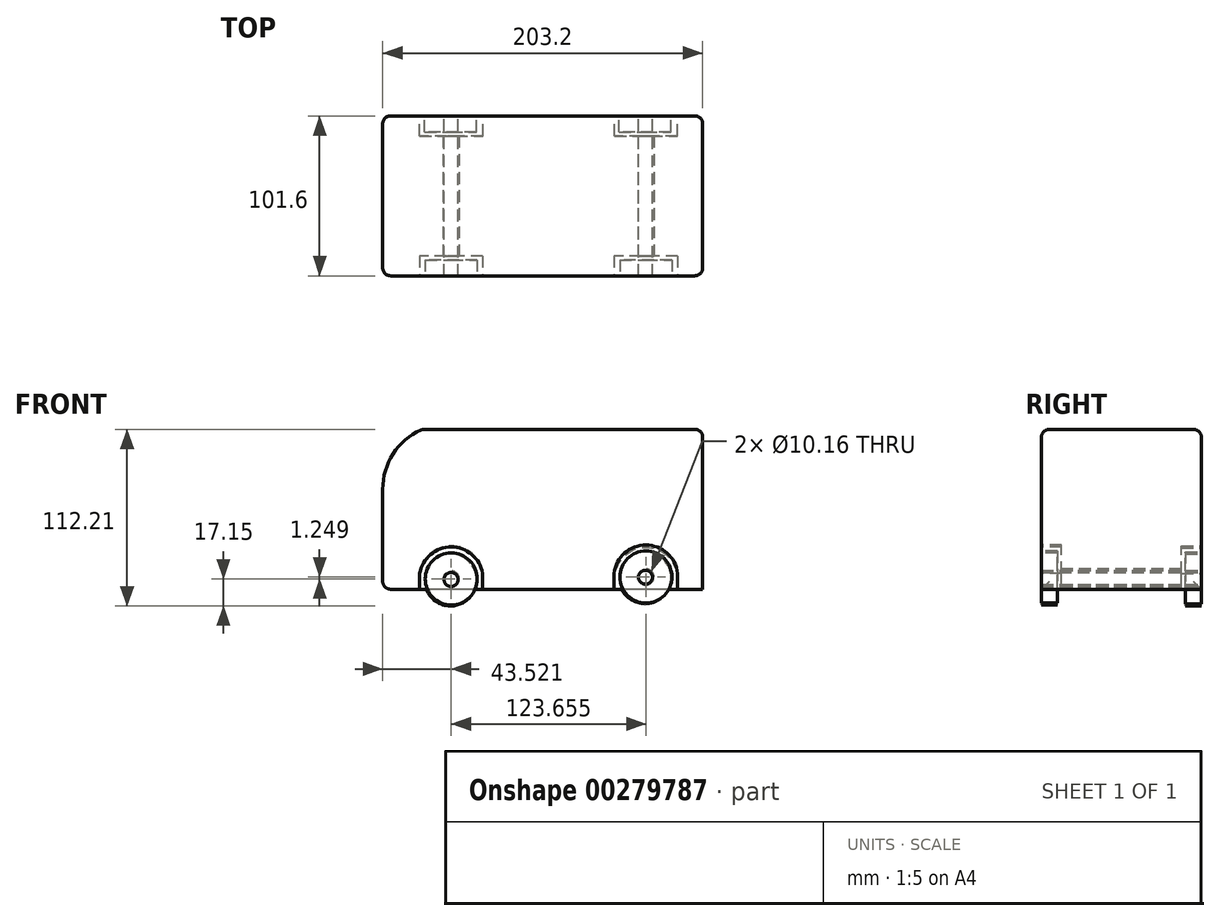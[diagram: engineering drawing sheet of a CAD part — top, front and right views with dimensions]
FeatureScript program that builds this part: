
annotation { "Feature Type Name" : "Feature", "Feature Type Description" : "" }
export const myFeature = defineFeature(function(context is Context, id is Id, definition is map)
    precondition{}
    {
        {
            var Q0;
            Q0=qCreatedBy(makeId("Front.planeOp"),FACE);
            var sketch = newSketch(context, id + "F0", { "sketchPlane" : qUnion([Q0])});
            skLineSegment(sketch, "E0", {"start": v(58.5, 0) * mm, "end": v(58.5, 50.8) * mm});
            skLineSegment(sketch, "E1.MirrorCS", {"start": v(58.5, 0) * mm, "end": v(58.5, -50.8) * mm});
            skLineSegment(sketch, "E2", {"start": v(58.5, 50.8) * mm, "end": v(-119.3, 50.8) * mm});
            skLineSegment(sketch, "E3", {"start": v(58.5, -50.8) * mm, "end": v(-144.7, -50.8) * mm});
            skLineSegment(sketch, "E4", {"start": v(-144.7, -50.8) * mm, "end": v(-144.7, 12.7) * mm});
            skArc(sketch, "E5", {"start": v(-119.3, 50.8) * mm, "mid": v(-137.76, 35.6) * mm, "end": v(-144.7, 12.7) * mm});
            skSolve(sketch);
        }
        {
            var Q0;
            Q0 = qSketchRegion(id + "F0", true);
            extrude(context, id + "F1", {"entities" : qUnion([Q0]), "depth" : 101.6 * mm});
        }
        {
            var Q0;
            Q0=makeQuery(id+"F1.opExtrude","CAP_EDGE",EDGE,{"disambiguationData":[OSD([sQuery(id+"F0.wireOp",EDGE,"E2")])],"isStart":true});
            var Q1;
            Q1=makeQuery(id+"F1.opExtrude","SWEPT_EDGE",EDGE,{"disambiguationData":[OSD([sQuery(id+"F0.wireOp",EDGE,"E2"),sQuery(id+"F0.wireOp",EDGE,"E5")])]});
            var Q2;
            Q2=makeQuery(id+"F1.opExtrude","CAP_EDGE",EDGE,{"disambiguationData":[OSD([sQuery(id+"F0.wireOp",EDGE,"E5")])],"isStart":true});
            var Q3;
            Q3=makeQuery(id+"F1.opExtrude","CAP_EDGE",EDGE,{"disambiguationData":[OSD([sQuery(id+"F0.wireOp",EDGE,"E4")])],"isStart":true});
            var Q4;
            Q4=makeQuery(id+"F1.opExtrude","CAP_EDGE",EDGE,{"disambiguationData":[OSD([sQuery(id+"F0.wireOp",EDGE,"E4")])],"isStart":false});
            var Q5;
            Q5=makeQuery(id+"F1.opExtrude","CAP_EDGE",EDGE,{"disambiguationData":[OSD([sQuery(id+"F0.wireOp",EDGE,"E5")])],"isStart":false});
            var Q6;
            Q6=makeQuery(id+"F1.opExtrude","CAP_EDGE",EDGE,{"disambiguationData":[OSD([sQuery(id+"F0.wireOp",EDGE,"E2")])],"isStart":false});
            var Q7;
            Q7=makeQuery(id+"F1.opExtrude","SWEPT_EDGE",EDGE,{"disambiguationData":[OSD([sQuery(id+"F0.wireOp",EDGE,"E0"),sQuery(id+"F0.wireOp",EDGE,"E2")])]});
            var Q8;
            Q8=makeQuery(id+"F1.opExtrude","CAP_EDGE",EDGE,{"disambiguationData":[OSD([sQuery(id+"F0.wireOp",EDGE,"E0"),sQuery(id+"F0.wireOp",EDGE,"E1.MirrorCS")])],"isStart":true});
            var Q9;
            Q9=makeQuery(id+"F1.opExtrude","CAP_EDGE",EDGE,{"disambiguationData":[OSD([sQuery(id+"F0.wireOp",EDGE,"E0"),sQuery(id+"F0.wireOp",EDGE,"E1.MirrorCS")])],"isStart":false});
            var Q10;
            Q10=makeQuery(id+"F1.opExtrude","SWEPT_EDGE",EDGE,{"disambiguationData":[OSD([sQuery(id+"F0.wireOp",EDGE,"E3"),sQuery(id+"F0.wireOp",EDGE,"E4")])]});
            fillet(context, id + "F2", {"entities" : qUnion([Q0, Q1, Q2, Q3, Q4, Q5, Q6, Q7, Q8, Q9, Q10]), "radius" : 5.08 * mm, "tangentPropagation" : true, "allowEdgeOverflow" : false});
        }
        {
            var Q0;
            Q0=makeQuery(id+"F1.opExtrude","CAP_FACE",FACE,{"disambiguationData":[OSD([sQuery(id+"F0.wireOp",EDGE,"E0"),sQuery(id+"F0.wireOp",EDGE,"E1.MirrorCS"),sQuery(id+"F0.wireOp",EDGE,"E2"),sQuery(id+"F0.wireOp",EDGE,"E3"),sQuery(id+"F0.wireOp",EDGE,"E4"),sQuery(id+"F0.wireOp",EDGE,"E5")])],"isStart":false});
            var sketch = newSketch(context, id + "F3", { "sketchPlane" : qUnion([Q0])});
            skLineSegment(sketch, "E6", {"start": v(-121.16, -50.8) * mm, "end": v(-121.16, -40.64) * mm});
            skLineSegment(sketch, "E7", {"start": v(-81.17, -50.8) * mm, "end": v(-81.17, -40.64) * mm});
            skArc(sketch, "E8", {"start": v(-81.17, -40.64) * mm, "mid": v(-101.17, -23.94) * mm, "end": v(-121.16, -40.64) * mm});
            skLineSegment(sketch, "E9", {"start": v(2.3, -50.8) * mm, "end": v(2.3, -40.64) * mm});
            skLineSegment(sketch, "E10", {"start": v(42.67, -50.8) * mm, "end": v(42.67, -40.64) * mm});
            skArc(sketch, "E11", {"start": v(42.67, -40.64) * mm, "mid": v(22.49, -22.7) * mm, "end": v(2.3, -40.64) * mm});
            skCircle(sketch, "E12", {"center": v(-101.17, -44.26) * mm, "radius": 5.08 * mm});
            skCircle(sketch, "E13", {"center": v(22.49, -43.01) * mm, "radius": 5.08 * mm});
            skSolve(sketch);
        }
        {
            var Q0;
            {var subQ1=sQuery(id+"F3.wireOp",EDGE,"E6");Q0=makeQuery(id+"F3.imprint","IMPRINT",FACE,{"disambiguationData":[TD([[makeQuery(id+"F3.imprint","IMPRINT",EDGE,{"derivedFrom":subQ1}),-1.0]])]});}
            var Q1;
            {var subQ0=sQuery(id+"F3.wireOp",EDGE,"E9");Q1=makeQuery(id+"F3.imprint","IMPRINT",FACE,{"disambiguationData":[TD([[makeQuery(id+"F3.imprint","IMPRINT",EDGE,{"derivedFrom":subQ0}),-1.0]])]});}
            extrude(context, id + "F4", {"entities" : qUnion([Q0, Q1]), "operationType" : NewBodyOperationType.REMOVE, "oppositeDirection" : true, "depth" : 12.7 * mm});
        }
        {
            var Q0;
            Q0=makeQuery(id+"F4.boolean.opBoolean","SPLIT",FACE,{"disambiguationData":[TD([makeQuery(id+"F4.opExtrude","SWEPT_FACE",FACE,{"disambiguationData":[OSD([sQuery(id+"F3.wireOp",EDGE,"E12")])]})])],"derivedFrom":makeQuery(id+"F1.opExtrude","CAP_FACE",FACE,{"disambiguationData":[OSD([sQuery(id+"F0.wireOp",EDGE,"E0"),sQuery(id+"F0.wireOp",EDGE,"E1.MirrorCS"),sQuery(id+"F0.wireOp",EDGE,"E2"),sQuery(id+"F0.wireOp",EDGE,"E3"),sQuery(id+"F0.wireOp",EDGE,"E4"),sQuery(id+"F0.wireOp",EDGE,"E5")])],"isStart":false})});
            var Q1;
            Q1=makeQuery(id+"F4.boolean.opBoolean","SPLIT",FACE,{"disambiguationData":[TD([makeQuery(id+"F4.opExtrude","SWEPT_FACE",FACE,{"disambiguationData":[OSD([sQuery(id+"F3.wireOp",EDGE,"E13")])]})])],"derivedFrom":makeQuery(id+"F1.opExtrude","CAP_FACE",FACE,{"disambiguationData":[OSD([sQuery(id+"F0.wireOp",EDGE,"E0"),sQuery(id+"F0.wireOp",EDGE,"E1.MirrorCS"),sQuery(id+"F0.wireOp",EDGE,"E2"),sQuery(id+"F0.wireOp",EDGE,"E3"),sQuery(id+"F0.wireOp",EDGE,"E4"),sQuery(id+"F0.wireOp",EDGE,"E5")])],"isStart":false})});
            extrude(context, id + "F5", {"entities" : qUnion([Q0, Q1]), "operationType" : NewBodyOperationType.REMOVE, "oppositeDirection" : true, "depth" : 101.6 * mm});
        }
        {
            var Q0;
            Q0=makeQuery(id+"F1.opExtrude","CAP_FACE",FACE,{"disambiguationData":[OSD([sQuery(id+"F0.wireOp",EDGE,"E0"),sQuery(id+"F0.wireOp",EDGE,"E1.MirrorCS"),sQuery(id+"F0.wireOp",EDGE,"E2"),sQuery(id+"F0.wireOp",EDGE,"E3"),sQuery(id+"F0.wireOp",EDGE,"E4"),sQuery(id+"F0.wireOp",EDGE,"E5")])],"isStart":true});
            var sketch = newSketch(context, id + "F6", { "sketchPlane" : qUnion([Q0])});
            skLineSegment(sketch, "E14", {"start": v(-17.58, -41.7) * mm, "end": v(-2.6, -41.7) * mm});
            skLineSegment(sketch, "E15", {"start": v(106.24, -44.03) * mm, "end": v(121.23, -44.03) * mm});
            skLineSegment(sketch, "E16", {"start": v(-27.55, -42.64) * mm, "end": v(-42.54, -42.64) * mm});
            skLineSegment(sketch, "E17", {"start": v(96.1, -44.1) * mm, "end": v(81.1, -44.1) * mm});
            skLineSegment(sketch, "E18", {"start": v(-42.54, -50.8) * mm, "end": v(-42.54, -40.64) * mm});
            skLineSegment(sketch, "E19", {"start": v(-2.6, -50.8) * mm, "end": v(-2.6, -40.64) * mm});
            skLineSegment(sketch, "E20", {"start": v(81.1, -50.8) * mm, "end": v(81.1, -40.64) * mm});
            skLineSegment(sketch, "E21", {"start": v(121.23, -50.8) * mm, "end": v(121.23, -40.64) * mm});
            skArc(sketch, "E22", {"start": v(-2.6, -40.64) * mm, "mid": v(-22.57, -24.45) * mm, "end": v(-42.54, -40.64) * mm});
            skArc(sketch, "E23", {"start": v(121.23, -40.64) * mm, "mid": v(101.17, -23.2) * mm, "end": v(81.1, -40.64) * mm});
            skSolve(sketch);
        }
        {
            var Q0;
            {var subQ1=sQuery(id+"F6.wireOp",EDGE,"E14");Q0=makeQuery(id+"F6.imprint","IMPRINT",FACE,{"disambiguationData":[TD([[makeQuery(id+"F6.imprint","IMPRINT",EDGE,{"derivedFrom":subQ1}),-1.0]])]});}
            var Q1;
            {var subQ1=sQuery(id+"F6.wireOp",EDGE,"E15");Q1=makeQuery(id+"F6.imprint","IMPRINT",FACE,{"disambiguationData":[TD([[makeQuery(id+"F6.imprint","IMPRINT",EDGE,{"derivedFrom":subQ1}),-1.0]])]});}
            var Q2;
            {var subQ4=sQuery(id+"F6.wireOp",EDGE,"E15");Q2=makeQuery(id+"F6.imprint","IMPRINT",FACE,{"disambiguationData":[TD([[makeQuery(id+"F6.imprint","IMPRINT",EDGE,{"derivedFrom":subQ4}),1.0]])]});}
            var Q3;
            {var subQ1=sQuery(id+"F6.wireOp",EDGE,"E14");Q3=makeQuery(id+"F6.imprint","IMPRINT",FACE,{"disambiguationData":[TD([[makeQuery(id+"F6.imprint","IMPRINT",EDGE,{"derivedFrom":subQ1}),1.0]])]});}
            var Q4;
            Q4=sQuery(id+"F6.wireOp",EDGE,"E19");
            var Q5;
            Q5=sQuery(id+"F6.wireOp",EDGE,"E18");
            var Q6;
            Q6=sQuery(id+"F6.wireOp",EDGE,"E22");
            var Q7;
            Q7=sQuery(id+"F6.wireOp",EDGE,"E20");
            var Q8;
            Q8=sQuery(id+"F6.wireOp",EDGE,"E23");
            var Q9;
            Q9=sQuery(id+"F6.wireOp",EDGE,"E21");
            extrude(context, id + "F7", {"entities" : qUnion([Q0, Q1, Q2, Q3]), "operationType" : NewBodyOperationType.REMOVE, "surfaceEntities" : qUnion([Q4, Q5, Q6, Q7, Q8, Q9]), "oppositeDirection" : true, "depth" : 12.7 * mm});
        }
        {
            var Q0;
            Q0=qCreatedBy(makeId("Front.planeOp"),FACE);
            var sketch = newSketch(context, id + "F8", { "sketchPlane" : qUnion([Q0])});
            skCircle(sketch, "E24", {"center": v(-101.3, -44.6) * mm, "radius": 4.45 * mm});
            skCircle(sketch, "E25", {"center": v(22.16, -43.17) * mm, "radius": 4.45 * mm});
            skSolve(sketch);
        }
        {
            var Q0;
            Q0 = qSketchRegion(id + "F8", true);
            extrude(context, id + "F9", {"entities" : qUnion([Q0]), "depth" : 101.6 * mm});
        }
        {
            var Q0;
            Q0 = qSketchRegion(id + "F8", true);
            extrude(context, id + "F10", {"entities" : qUnion([Q0]), "depth" : 101.6 * mm});
        }
        {
            var Q0;
            Q0=qCreatedBy(makeId("Front.planeOp"),FACE);
            var sketch = newSketch(context, id + "F11", { "sketchPlane" : qUnion([Q0])});
            skCircle(sketch, "E26", {"center": v(-101.6, -44.9) * mm, "radius": 16.51 * mm});
            skCircle(sketch, "E27", {"center": v(21.88, -43.46) * mm, "radius": 16.51 * mm});
            skSolve(sketch);
        }
        {
            var Q0;
            Q0=makeQuery(id+"F11.imprint","IMPRINT",FACE,{"disambiguationData":[TD([[makeQuery(id+"F11.imprint","IMPRINT",EDGE,{"derivedFrom":sQuery(id+"F11.wireOp",EDGE,"E27")}),1.0]])]});
            var Q1;
            Q1=makeQuery(id+"F11.imprint","IMPRINT",FACE,{"disambiguationData":[TD([[makeQuery(id+"F11.imprint","IMPRINT",EDGE,{"derivedFrom":sQuery(id+"F11.wireOp",EDGE,"E26")}),1.0]])]});
            var Q2;
            Q2=sQuery(id+"F11.wireOp",EDGE,"E26");
            var Q3;
            Q3=sQuery(id+"F11.wireOp",EDGE,"E27");
            extrude(context, id + "F12", {"entities" : qUnion([Q0, Q1]), "surfaceEntities" : qUnion([Q2, Q3]), "depth" : 10.16 * mm});
        }
        {
            var Q0;
            {var subQ0=sQuery(id+"F0.wireOp",EDGE,"E2");var subQ1=sQuery(id+"F0.wireOp",EDGE,"E1.MirrorCS");var subQ2=sQuery(id+"F0.wireOp",EDGE,"E0");var subQ3=sQuery(id+"F0.wireOp",EDGE,"E3");var subQ4=sQuery(id+"F0.wireOp",EDGE,"E5");var subQ5=sQuery(id+"F0.wireOp",EDGE,"E4");Q0=makeQuery(id+"F4.boolean.opBoolean","SPLIT",FACE,{"disambiguationData":[TD([makeQuery(id+"F1.opExtrude","SWEPT_FACE",FACE,{"disambiguationData":[OSD([subQ3])]})])],"derivedFrom":makeQuery(id+"F1.opExtrude","CAP_FACE",FACE,{"disambiguationData":[OSD([subQ2,subQ1,subQ0,subQ3,subQ5,subQ4])],"isStart":false})});}
            var sketch = newSketch(context, id + "F13", { "sketchPlane" : qUnion([Q0])});
            skCircle(sketch, "E28", {"center": v(-101.17, -44.26) * mm, "radius": 16.51 * mm});
            skCircle(sketch, "E29", {"center": v(22.49, -43.01) * mm, "radius": 16.51 * mm});
            skSolve(sketch);
        }
        {
            var Q0;
            Q0=makeQuery(id+"F13.imprint","IMPRINT",FACE,{"disambiguationData":[TD([[makeQuery(id+"F13.imprint","IMPRINT",EDGE,{"derivedFrom":sQuery(id+"F13.wireOp",EDGE,"E28")}),1.0]])]});
            var Q1;
            Q1=makeQuery(id+"F13.imprint","IMPRINT",FACE,{"disambiguationData":[TD([[makeQuery(id+"F13.imprint","IMPRINT",EDGE,{"derivedFrom":sQuery(id+"F13.wireOp",EDGE,"E29")}),1.0]])]});
            extrude(context, id + "F14", {"entities" : qUnion([Q0, Q1]), "oppositeDirection" : true, "depth" : 10.16 * mm});
        }
    });
